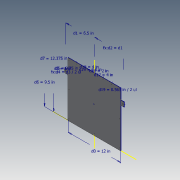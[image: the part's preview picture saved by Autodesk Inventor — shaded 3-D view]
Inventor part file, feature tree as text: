
AUTODESK INVENTOR PART (.ipt)
format: ipt  version: 2020.3 (Build 243373000, 373)  size: 168,448 bytes
history: native  units: in
note: dims shown in document units (in); Inventor stores cm internally (conversion verified against a paired STEP export)
features: hole x3, sketch x2, fillet x2, extrude x1
ambient origin geometry x8: Origin, YZ Plane, XZ Plane, XY Plane, X Axis, Y Axis, Z Axis, Center Point
bodies: Solid1 (feature_tree)
feature tree (8):
  sketch  "Sketch1"  dims[d0=12.0in d1=6.5in]
  extrude  "Extrusion1"  Depth=12.0in
  hole  "Hole1"  [1 undecoded]
  fillet  "Fillet1"  Radius=0.5in
  hole  "Hole2"  [1 undecoded]
  fillet  "Fillet2"  Radius=9.5in
  hole  "Hole3"  [1 undecoded]
  sketch  "Sketch2"  dims[d2=6.5in d3=1.0in d4=0.5in d5=0.75in d6=9.5in d7=12.375in d8=0.07in d9=0.0in d10=0.21in d11=0.75in d12=0.385in d13=0.25in d14=0.5635in d15=1.0in d16=0.8108in d17=4.0in d18=4.0in d19=0.2815in d20=0.125in d21=0.094in d22=0.75in d23=0.173in d24=0.25in d25=90.0deg d26=1.0in d27=0.8108in d28=0.25in d29=2.0in d30=2.0in d31=11.5in d32=11.5in d33=0.096in d34=0.75in d35=0.172in d36=0.25in d37=0.6871in d38=1.0in d39=0.0in]
note: 3 required parameter values undecoded (feature->parameter linkage not recoverable at this tier; creation-order binding heuristic only, values carry confidence <= 0.55)
